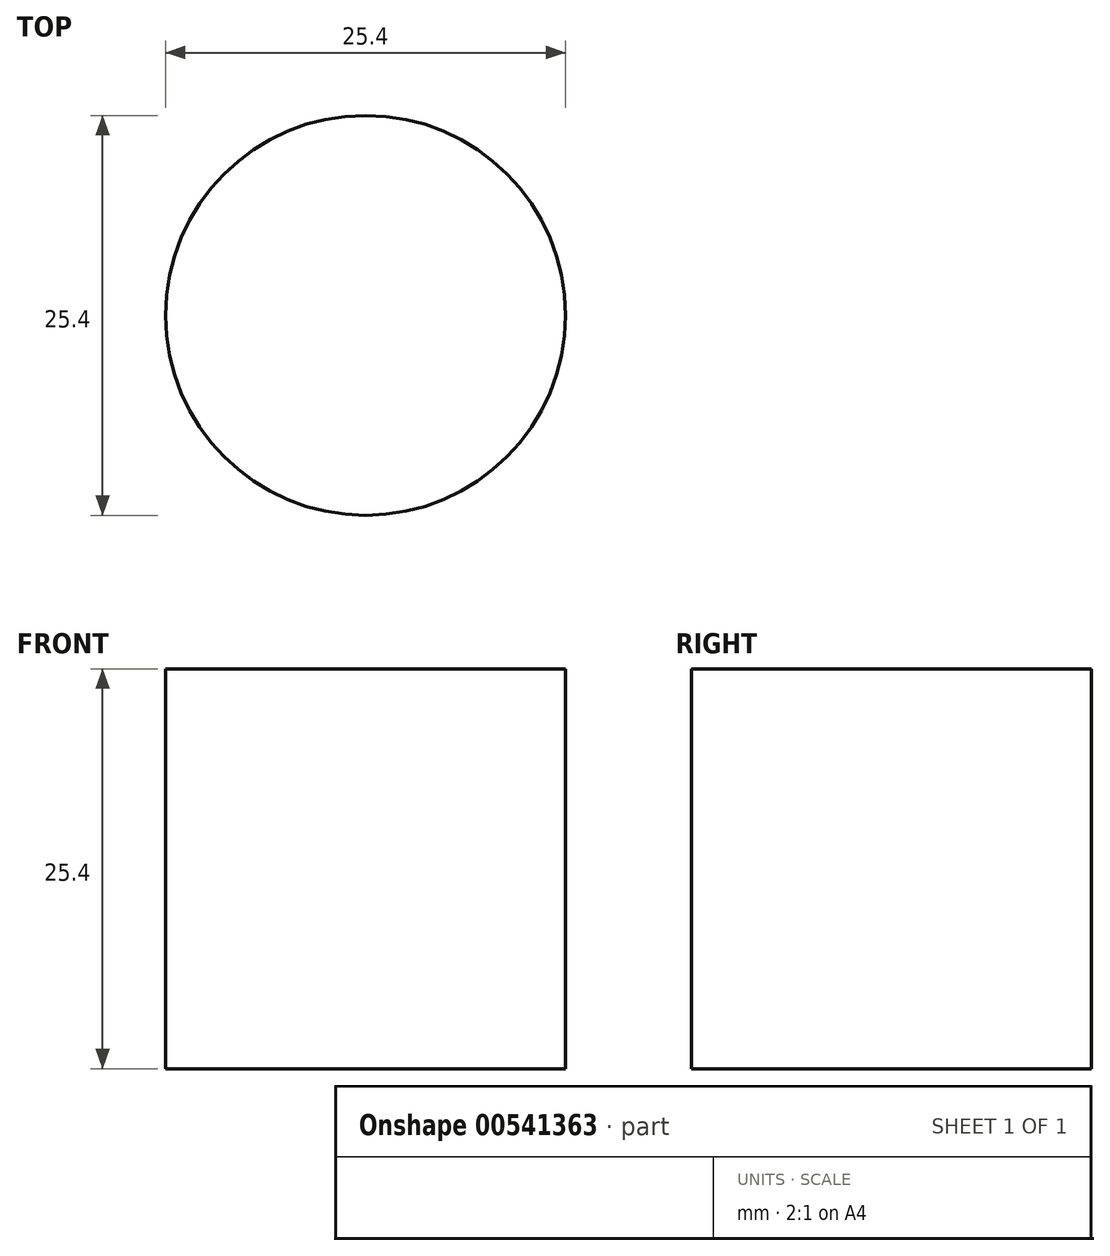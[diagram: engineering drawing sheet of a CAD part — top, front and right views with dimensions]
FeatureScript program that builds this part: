
annotation { "Feature Type Name" : "Feature", "Feature Type Description" : "" }
export const myFeature = defineFeature(function(context is Context, id is Id, definition is map)
    precondition{}
    {
        {
            var Q0;
            Q0=qCreatedBy(makeId("Top.planeOp"),FACE);
            var sketch = newSketch(context, id + "F0", { "sketchPlane" : qUnion([Q0])});
            skCircle(sketch, "E0", {"center": v(0, 0) * mm, "radius": 12.7 * mm});
            skSolve(sketch);
        }
        {
            var Q0;
            Q0=makeQuery(id+"F0.imprint","IMPRINT",FACE,{"disambiguationData":[TD([[makeQuery(id+"F0.imprint","IMPRINT",EDGE,{"derivedFrom":sQuery(id+"F0.wireOp",EDGE,"E0")}),1.0]])]});
            extrude(context, id + "F1", {"entities" : qUnion([Q0]), "depth" : 25.4 * mm, "offsetDistance" : 25.4 * mm});
        }
    });
